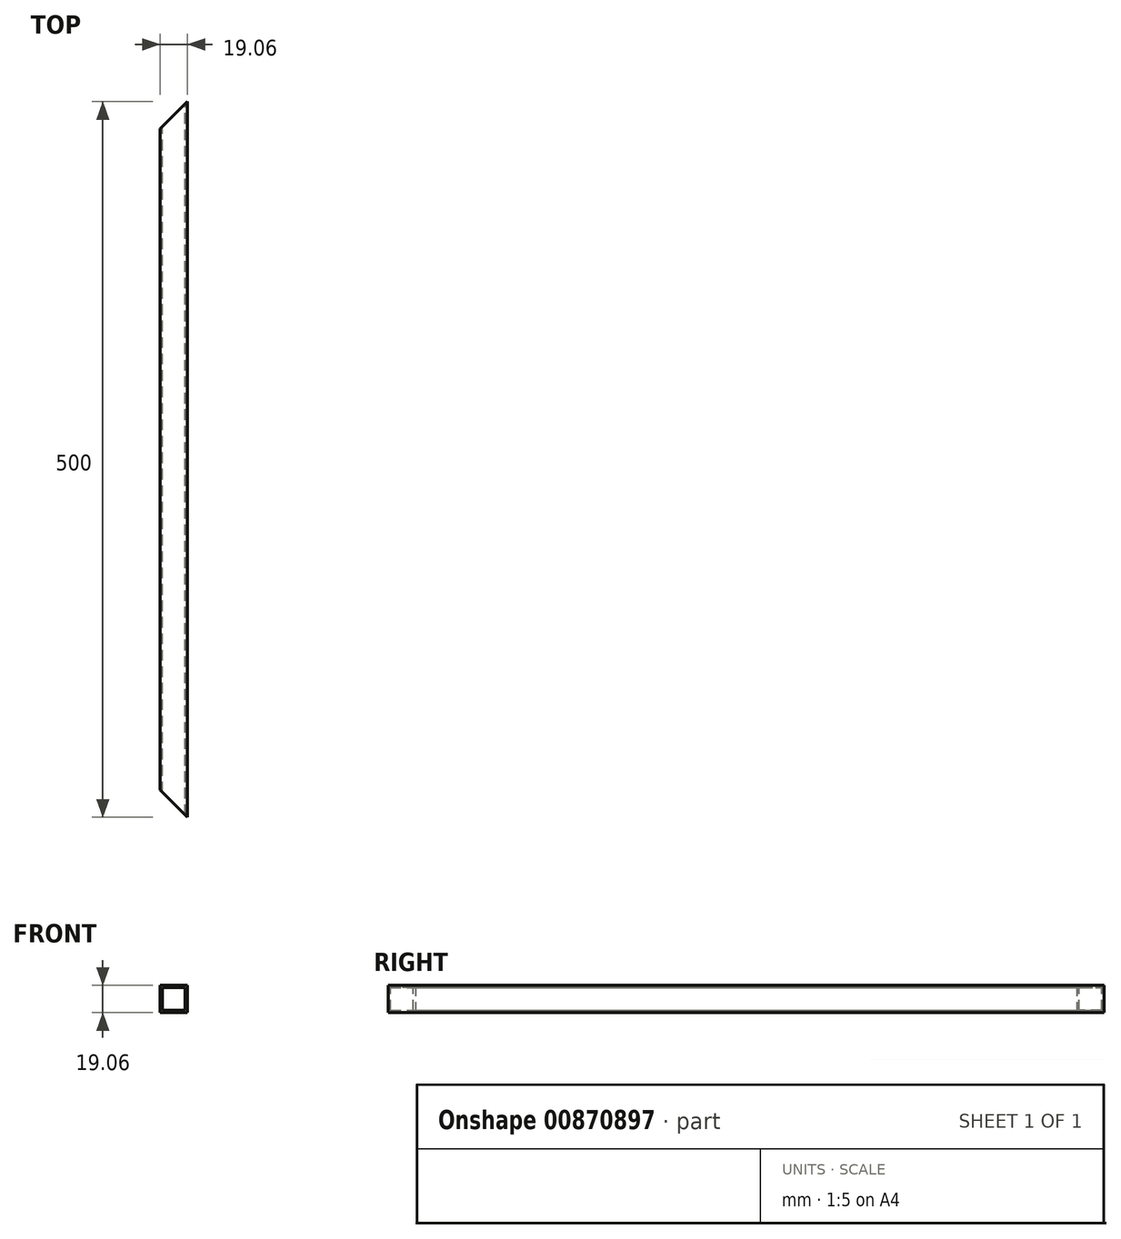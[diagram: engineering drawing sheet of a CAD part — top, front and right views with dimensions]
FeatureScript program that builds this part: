
annotation { "Feature Type Name" : "Feature", "Feature Type Description" : "" }
export const myFeature = defineFeature(function(context is Context, id is Id, definition is map)
    precondition{}
    {
        {
            var Q0;
            Q0=qCreatedBy(makeId("Front.planeOp"),FACE);
            var sketch = newSketch(context, id + "F0", { "sketchPlane" : qUnion([Q0])});
            skLineSegment(sketch, "E0.bottom", {"start": v(9.53, 9.53) * mm, "end": v(-9.53, 9.53) * mm});
            skLineSegment(sketch, "E0.top", {"start": v(9.53, -9.52) * mm, "end": v(-9.53, -9.52) * mm});
            skLineSegment(sketch, "E0.left", {"start": v(9.53, 9.53) * mm, "end": v(9.53, -9.52) * mm});
            skLineSegment(sketch, "E0.right", {"start": v(-9.53, 9.53) * mm, "end": v(-9.53, -9.52) * mm});
            skPoint(sketch, "E0.middle", {"position": v(0, 0) * mm});
            skLineSegment(sketch, "E1.bottom", {"start": v(7.94, 7.94) * mm, "end": v(-7.94, 7.94) * mm});
            skLineSegment(sketch, "E1.top", {"start": v(7.94, -7.94) * mm, "end": v(-7.94, -7.94) * mm});
            skLineSegment(sketch, "E1.left", {"start": v(7.94, 7.94) * mm, "end": v(7.94, -7.94) * mm});
            skLineSegment(sketch, "E1.right", {"start": v(-7.94, 7.94) * mm, "end": v(-7.94, -7.94) * mm});
            skSolve(sketch);
        }
        {
            var Q0;
            Q0 = qSketchRegion(id + "F0", true);
            extrude(context, id + "F1", {"entities" : qUnion([Q0]), "depth" : 500 * mm, "offsetDistance" : 25 * mm});
        }
        {
            var Q0;
            Q0=qCreatedBy(makeId("Top.planeOp"),FACE);
            var sketch = newSketch(context, id + "F2", { "sketchPlane" : qUnion([Q0])});
            skLineSegment(sketch, "E2", {"start": v(-9.53, 0) * mm, "end": v(9.53, 0) * mm});
            skLineSegment(sketch, "E3", {"start": v(-9.53, 0) * mm, "end": v(-9.53, -19.05) * mm});
            skLineSegment(sketch, "E4", {"start": v(-9.53, -19.05) * mm, "end": v(9.53, 0) * mm});
            skPoint(sketch, "E5", {"position": v(0, -500) * mm});
            skLineSegment(sketch, "E6", {"start": v(-9.52, -500) * mm, "end": v(9.52, -500) * mm});
            skLineSegment(sketch, "E7", {"start": v(-9.53, -500) * mm, "end": v(-9.53, -480.95) * mm});
            skLineSegment(sketch, "E8", {"start": v(-9.52, -480.95) * mm, "end": v(9.53, -500) * mm});
            skSolve(sketch);
        }
        {
            var Q0;
            Q0 = qSketchRegion(id + "F2", true);
            extrude(context, id + "F3", {"entities" : qUnion([Q0]), "operationType" : NewBodyOperationType.REMOVE, "endBound" : BoundingType.THROUGH_ALL, "depth" : 25 * mm, "offsetDistance" : 25 * mm});
        }
        {
            var Q0;
            Q0 = qSketchRegion(id + "F2", true);
            extrude(context, id + "F4", {"entities" : qUnion([Q0]), "operationType" : NewBodyOperationType.REMOVE, "endBound" : BoundingType.THROUGH_ALL, "oppositeDirection" : true, "depth" : 25 * mm, "offsetDistance" : 25 * mm});
        }
    });
